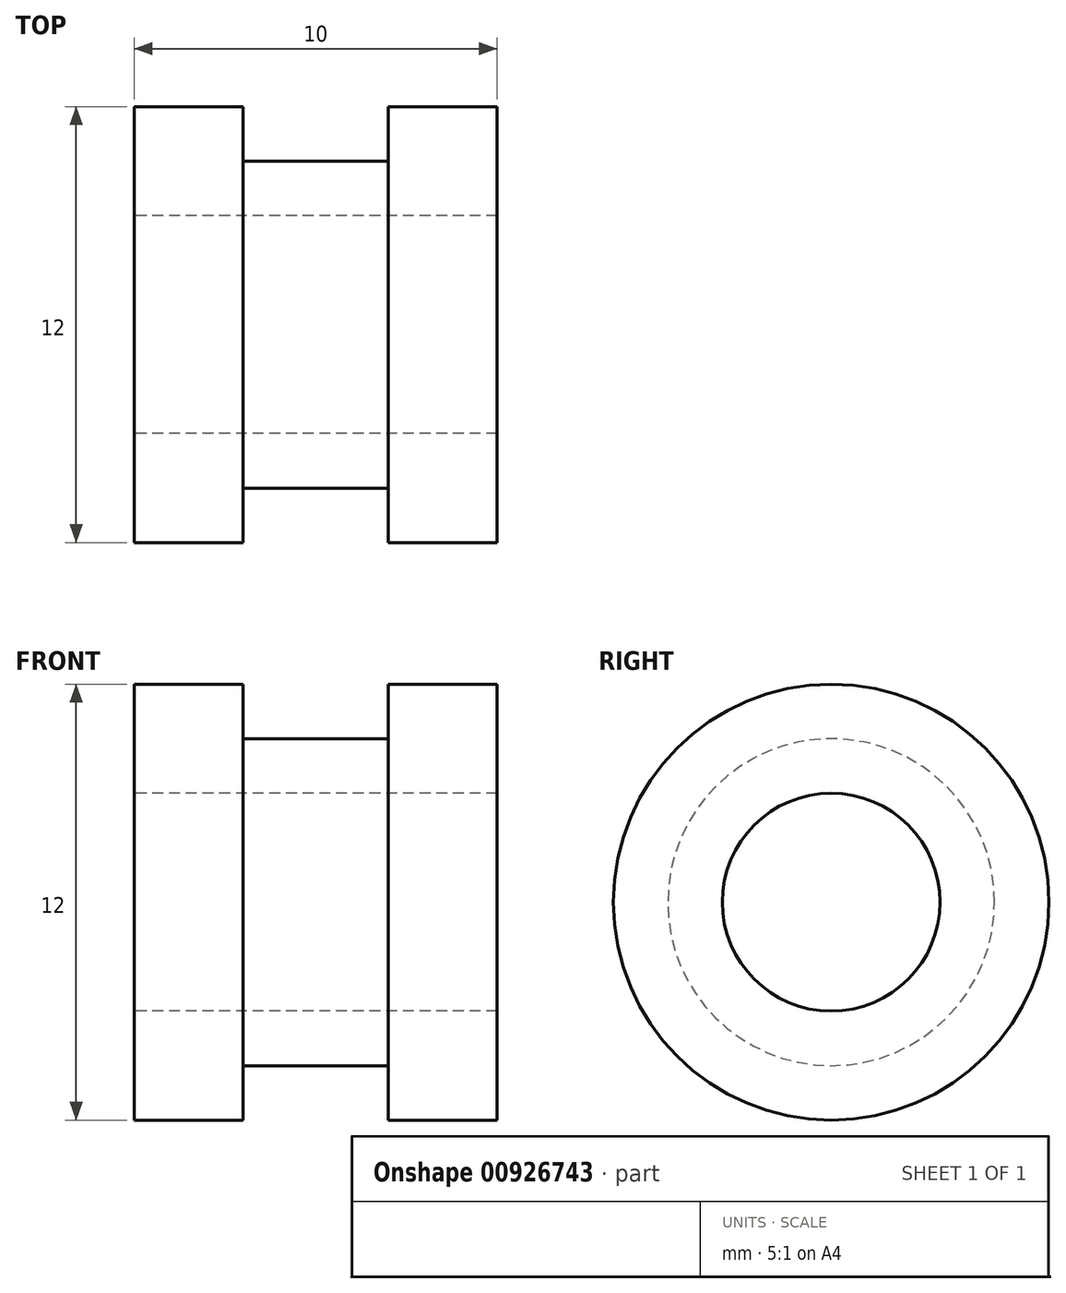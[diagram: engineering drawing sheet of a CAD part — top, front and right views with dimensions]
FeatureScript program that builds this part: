
annotation { "Feature Type Name" : "Feature", "Feature Type Description" : "" }
export const myFeature = defineFeature(function(context is Context, id is Id, definition is map)
    precondition{}
    {
        {
            var Q0;
            Q0=qCreatedBy(makeId("Front.planeOp"),FACE);
            var sketch = newSketch(context, id + "F0", { "sketchPlane" : qUnion([Q0])});
            skLineSegment(sketch, "E0", {"start": v(0, 3) * mm, "end": v(10, 3) * mm});
            skLineSegment(sketch, "E1", {"start": v(10, 3) * mm, "end": v(10, 6) * mm});
            skLineSegment(sketch, "E2", {"start": v(10, 6) * mm, "end": v(7, 6) * mm});
            skLineSegment(sketch, "E3", {"start": v(7, 6) * mm, "end": v(7, 4.5) * mm});
            skLineSegment(sketch, "E4", {"start": v(7, 4.5) * mm, "end": v(3, 4.5) * mm});
            skLineSegment(sketch, "E5", {"start": v(3, 4.5) * mm, "end": v(3, 6) * mm});
            skLineSegment(sketch, "E6", {"start": v(3, 6) * mm, "end": v(0, 6) * mm});
            skLineSegment(sketch, "E7", {"start": v(0, 6) * mm, "end": v(0, 3) * mm});
            skLineSegment(sketch, "E8", {"start": v(0, 0) * mm, "end": v(42.31, 0) * mm, "construction": true});
            skSolve(sketch);
        }
        {
            var Q0;
            Q0=makeQuery(id+"F0.imprint","IMPRINT",FACE,{"disambiguationData":[TD([[makeQuery(id+"F0.imprint","IMPRINT",EDGE,{"derivedFrom":sQuery(id+"F0.wireOp",EDGE,"E0")}),1.0]])]});
            var Q1;
            Q1=sQuery(id+"F0.wireOp",EDGE,"E8");
            revolve(context, id + "F1", {"surfaceOperationType" : NewSurfaceOperationType.NEW, "entities" : qUnion([Q0]), "axis" : qUnion([Q1]), "revolveType" : RevolveType.FULL});
        }
    });
